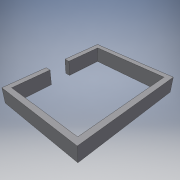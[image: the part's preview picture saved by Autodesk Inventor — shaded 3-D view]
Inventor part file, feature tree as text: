
AUTODESK INVENTOR PART (.ipt)
format: ipt  version: 2016 (Build 200138000, 138)  size: 104,960 bytes
history: native  units: in
note: dims shown in document units (in); Inventor stores cm internally (conversion verified against a paired STEP export)
features: extrude x2, sketch x2
ambient origin geometry x8: Origin, YZ Plane, XZ Plane, XY Plane, X Axis, Y Axis, Z Axis, Center Point
bodies: Solid1 (feature_tree)
feature tree (4):
  extrude  "Extrusion1"  Depth=16.0in
  extrude  "Extrusion2"  Depth=18.0in
  sketch  "Sketch1"  dims[d0=20.0in d1=16.0in]
  sketch  "Sketch2"  dims[d2=2.8in d3=0.0in d4=18.0in d5=14.0in d6=4.0in d7=2.8in d8=0.0in]
